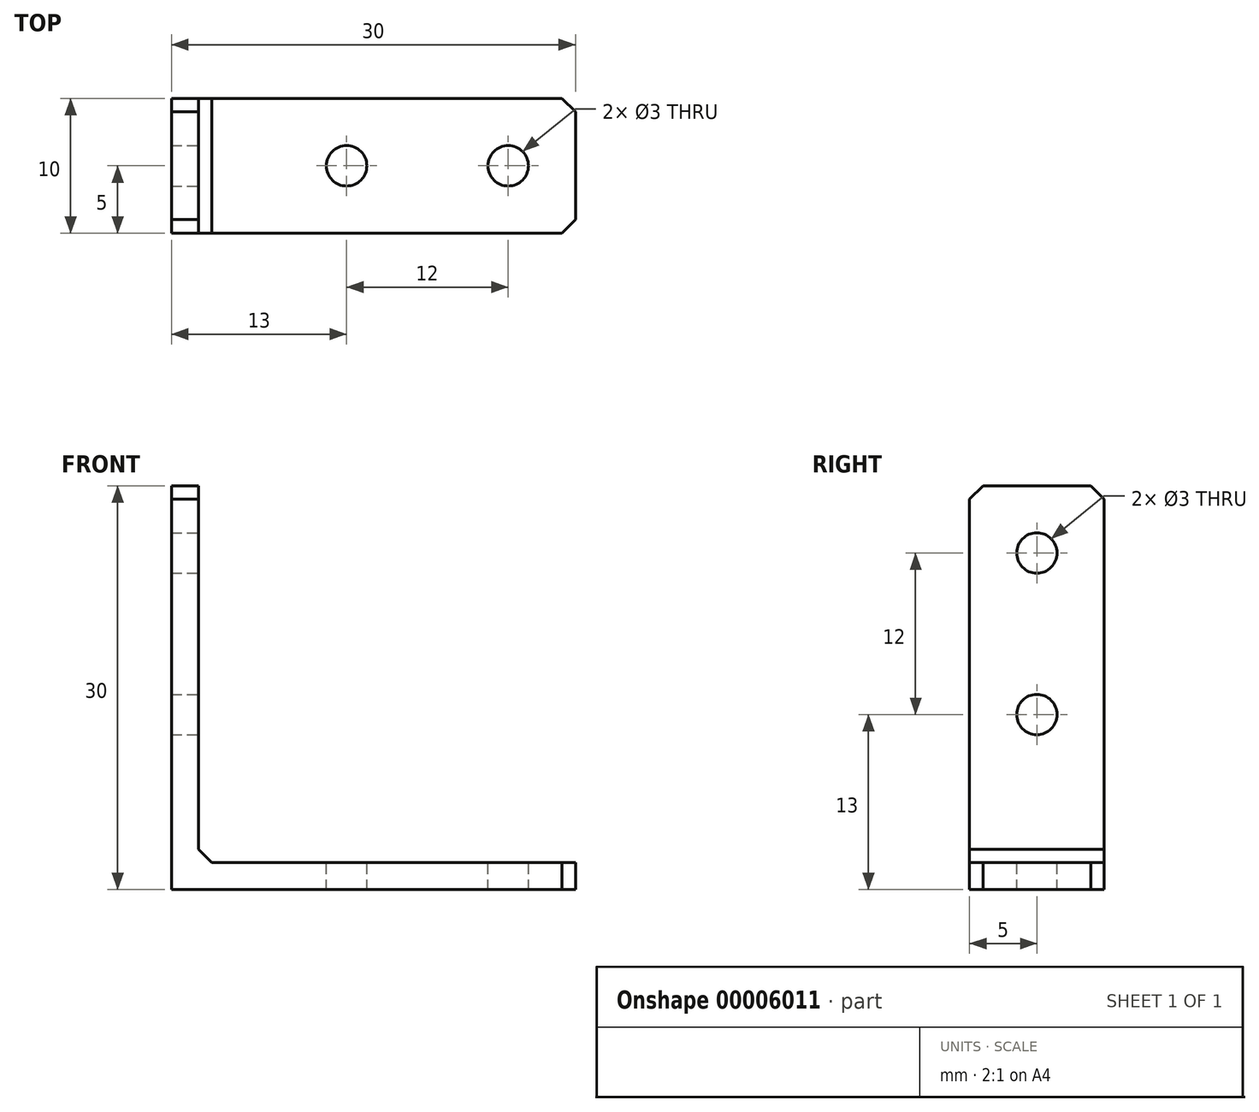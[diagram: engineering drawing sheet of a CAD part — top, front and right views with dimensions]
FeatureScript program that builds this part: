
annotation { "Feature Type Name" : "Feature", "Feature Type Description" : "" }
export const myFeature = defineFeature(function(context is Context, id is Id, definition is map)
    precondition{}
    {
        {
            var Q0;
            Q0=qCreatedBy(makeId("Front.planeOp"),FACE);
            var sketch = newSketch(context, id + "F0", { "sketchPlane" : qUnion([Q0])});
            skLineSegment(sketch, "E0.top", {"start": v(0, 30) * mm, "end": v(2, 30) * mm});
            skLineSegment(sketch, "E0.left", {"start": v(0, 0) * mm, "end": v(0, 30) * mm});
            skLineSegment(sketch, "E0.right", {"start": v(2, 2) * mm, "end": v(2, 30) * mm});
            skLineSegment(sketch, "E1.top", {"start": v(2, 2) * mm, "end": v(30, 2) * mm});
            skLineSegment(sketch, "E1.right", {"start": v(30, 0) * mm, "end": v(30, 2) * mm});
            skLineSegment(sketch, "E2", {"start": v(0, 0) * mm, "end": v(30, 0) * mm});
            skSolve(sketch);
        }
        {
            var Q0;
            Q0=makeQuery(id+"F0.imprint","IMPRINT",FACE,{"disambiguationData":[TD([[makeQuery(id+"F0.imprint","IMPRINT",EDGE,{"derivedFrom":sQuery(id+"F0.wireOp",EDGE,"E0.top")}),-1.0]])]});
            extrude(context, id + "F1", {"entities" : qUnion([Q0]), "depth" : 10 * mm});
        }
        {
            var Q0;
            Q0=makeQuery(id+"F1.opExtrude","CAP_EDGE",EDGE,{"disambiguationData":[OSD([sQuery(id+"F0.wireOp",EDGE,"E0.top")])],"isStart":false});
            var Q1;
            Q1=makeQuery(id+"F1.opExtrude","CAP_EDGE",EDGE,{"disambiguationData":[OSD([sQuery(id+"F0.wireOp",EDGE,"E0.top")])],"isStart":true});
            var Q2;
            Q2=makeQuery(id+"F1.opExtrude","CAP_EDGE",EDGE,{"disambiguationData":[OSD([sQuery(id+"F0.wireOp",EDGE,"E1.right")])],"isStart":false});
            var Q3;
            Q3=makeQuery(id+"F1.opExtrude","CAP_EDGE",EDGE,{"disambiguationData":[OSD([sQuery(id+"F0.wireOp",EDGE,"E1.right")])],"isStart":true});
            var Q4;
            Q4=makeQuery(id+"F1.opExtrude","SWEPT_EDGE",EDGE,{"disambiguationData":[OSD([sQuery(id+"F0.wireOp",EDGE,"E0.right"),sQuery(id+"F0.wireOp",EDGE,"E1.top")])]});
            chamfer(context, id + "F2", {"entities" : qUnion([Q0, Q1, Q2, Q3, Q4]), "width" : 1 * mm, "tangentPropagation" : true});
        }
        {
            var Q0;
            Q0=makeQuery(id+"F1.opExtrude","SWEPT_FACE",FACE,{"disambiguationData":[OSD([sQuery(id+"F0.wireOp",EDGE,"E1.top")])]});
            var sketch = newSketch(context, id + "F3", { "sketchPlane" : qUnion([Q0])});
            skLineSegment(sketch, "E3", {"start": v(30, -5) * mm, "end": v(0, -5) * mm, "construction": true});
            skCircle(sketch, "E4", {"center": v(13, -5) * mm, "radius": 1.5 * mm});
            skCircle(sketch, "E5", {"center": v(25, -5) * mm, "radius": 1.5 * mm});
            skSolve(sketch);
        }
        {
            var Q0;
            Q0=makeQuery(id+"F3.imprint","IMPRINT",FACE,{"disambiguationData":[TD([[makeQuery(id+"F3.imprint","IMPRINT",EDGE,{"derivedFrom":sQuery(id+"F3.wireOp",EDGE,"E4")}),1.0]])]});
            var Q1;
            Q1=makeQuery(id+"F3.imprint","IMPRINT",FACE,{"disambiguationData":[TD([[makeQuery(id+"F3.imprint","IMPRINT",EDGE,{"derivedFrom":sQuery(id+"F3.wireOp",EDGE,"E5")}),1.0]])]});
            var Q2;
            Q2=sQuery(id+"F3.wireOp",EDGE,"E4");
            var Q3;
            Q3=sQuery(id+"F3.wireOp",EDGE,"E5");
            extrude(context, id + "F4", {"entities" : qUnion([Q0, Q1]), "operationType" : NewBodyOperationType.REMOVE, "surfaceEntities" : qUnion([Q2, Q3]), "endBound" : BoundingType.THROUGH_ALL, "oppositeDirection" : true, "depth" : 20 * mm});
        }
        {
            var Q0;
            Q0=makeQuery(id+"F1.opExtrude","SWEPT_FACE",FACE,{"disambiguationData":[OSD([sQuery(id+"F0.wireOp",EDGE,"E0.right")])]});
            var sketch = newSketch(context, id + "F5", { "sketchPlane" : qUnion([Q0])});
            skLineSegment(sketch, "E6", {"start": v(-5, 30) * mm, "end": v(-5, 0) * mm, "construction": true});
            skCircle(sketch, "E7", {"center": v(-5, 25) * mm, "radius": 1.5 * mm});
            skCircle(sketch, "E8", {"center": v(-5, 13) * mm, "radius": 1.5 * mm});
            skSolve(sketch);
        }
        {
            var Q0;
            Q0=makeQuery(id+"F5.imprint","IMPRINT",FACE,{"disambiguationData":[TD([[makeQuery(id+"F5.imprint","IMPRINT",EDGE,{"derivedFrom":sQuery(id+"F5.wireOp",EDGE,"E7")}),1.0]])]});
            var Q1;
            Q1=makeQuery(id+"F5.imprint","IMPRINT",FACE,{"disambiguationData":[TD([[makeQuery(id+"F5.imprint","IMPRINT",EDGE,{"derivedFrom":sQuery(id+"F5.wireOp",EDGE,"E8")}),1.0]])]});
            extrude(context, id + "F6", {"entities" : qUnion([Q0, Q1]), "operationType" : NewBodyOperationType.REMOVE, "endBound" : BoundingType.THROUGH_ALL, "oppositeDirection" : true, "depth" : 25 * mm});
        }
    });
